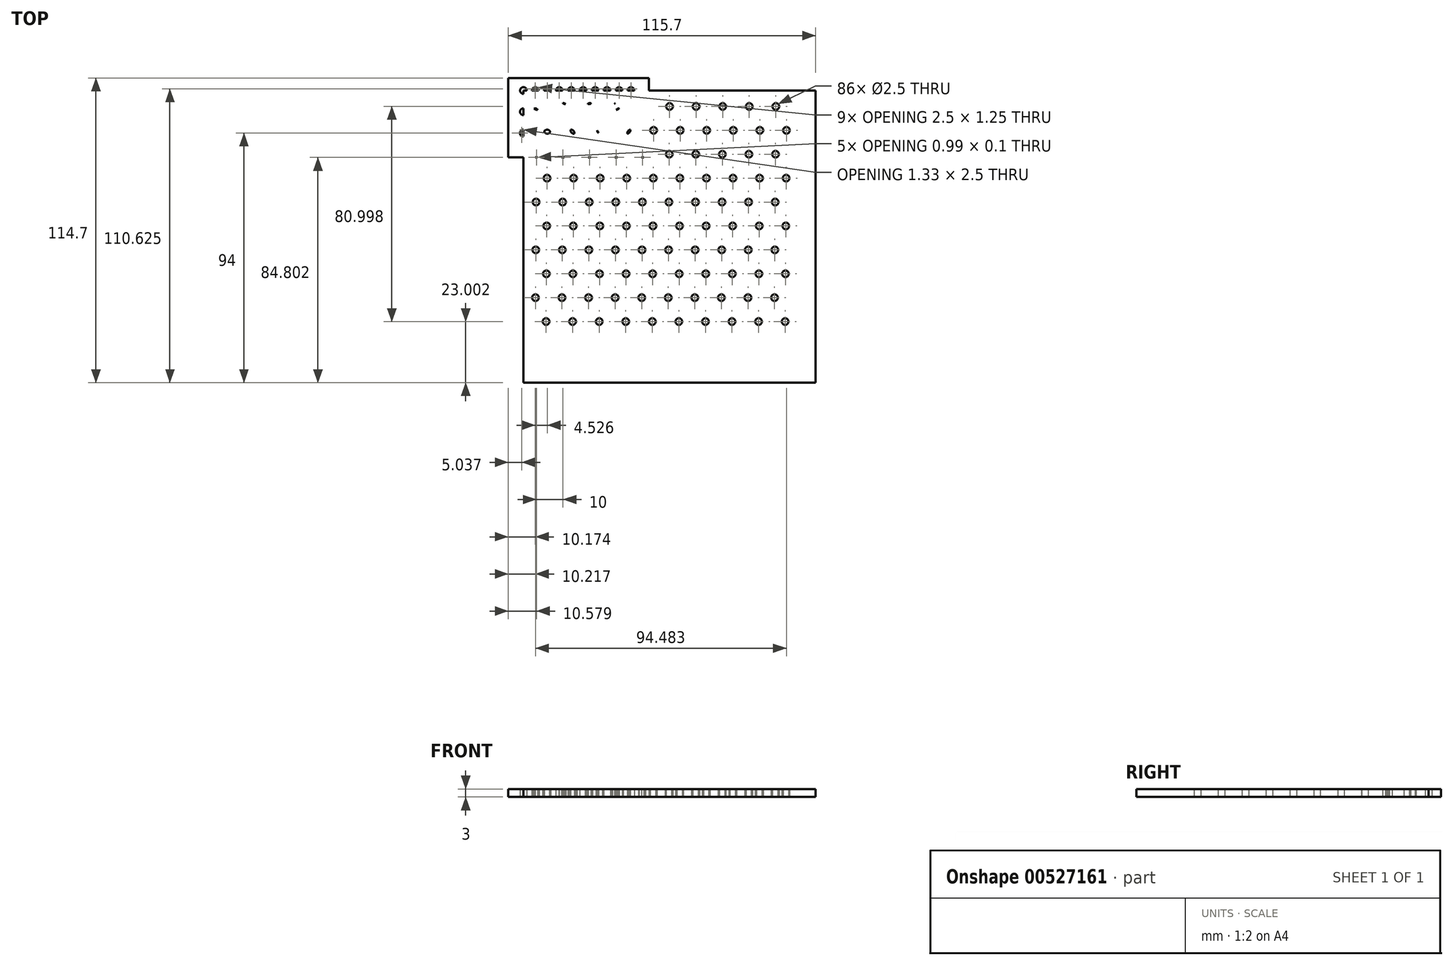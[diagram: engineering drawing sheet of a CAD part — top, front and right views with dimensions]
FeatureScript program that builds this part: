
annotation { "Feature Type Name" : "Feature", "Feature Type Description" : "" }
export const myFeature = defineFeature(function(context is Context, id is Id, definition is map)
    precondition{}
    {
        {
            var Q0;
            Q0=qCreatedBy(makeId("Top.planeOp"),FACE);
            var sketch = newSketch(context, id + "F0", { "sketchPlane" : qUnion([Q0])});
            skLineSegment(sketch, "E0.bottom", {"start": v(0, 0) * mm, "end": v(110, 0) * mm});
            skLineSegment(sketch, "E0.top", {"start": v(0, -110) * mm, "end": v(110, -110) * mm});
            skLineSegment(sketch, "E0.left", {"start": v(0, 0) * mm, "end": v(0, -110) * mm});
            skLineSegment(sketch, "E0.right", {"start": v(110, 0) * mm, "end": v(110, -110) * mm});
            skCircle(sketch, "E1", {"center": v(5, -6) * mm, "radius": 1.25 * mm});
            skCircle(sketch, "E2", {"center": v(9, -15) * mm, "radius": 1.25 * mm});
            skCircle(sketch, "E3", {"center": v(17.21, -30.05) * mm, "radius": 1.25 * mm});
            skCircle(sketch, "E4", {"center": v(38.99, -29.06) * mm, "radius": 1.25 * mm});
            skCircle(sketch, "E5.1.0.0", {"center": v(19, -15) * mm, "radius": 1.25 * mm});
            skCircle(sketch, "E5.1.0.1", {"center": v(15, -6) * mm, "radius": 1.25 * mm});
            skCircle(sketch, "E5.2.0.0", {"center": v(29, -15) * mm, "radius": 1.25 * mm});
            skCircle(sketch, "E5.2.0.1", {"center": v(25, -6) * mm, "radius": 1.25 * mm});
            skCircle(sketch, "E5.3.0.0", {"center": v(39, -15) * mm, "radius": 1.25 * mm});
            skCircle(sketch, "E5.3.0.1", {"center": v(35, -6) * mm, "radius": 1.25 * mm});
            skCircle(sketch, "E5.4.0.0", {"center": v(49, -15) * mm, "radius": 1.25 * mm});
            skCircle(sketch, "E5.4.0.1", {"center": v(45, -6) * mm, "radius": 1.25 * mm});
            skCircle(sketch, "E5.5.0.0", {"center": v(59, -15) * mm, "radius": 1.25 * mm});
            skCircle(sketch, "E5.5.0.1", {"center": v(55, -6) * mm, "radius": 1.25 * mm});
            skCircle(sketch, "E5.6.0.0", {"center": v(69, -15) * mm, "radius": 1.25 * mm});
            skCircle(sketch, "E5.6.0.1", {"center": v(65, -6) * mm, "radius": 1.25 * mm});
            skCircle(sketch, "E5.7.0.0", {"center": v(79, -15) * mm, "radius": 1.25 * mm});
            skCircle(sketch, "E5.7.0.1", {"center": v(75, -6) * mm, "radius": 1.25 * mm});
            skCircle(sketch, "E5.8.0.0", {"center": v(89, -15) * mm, "radius": 1.25 * mm});
            skCircle(sketch, "E5.8.0.1", {"center": v(85, -6) * mm, "radius": 1.25 * mm});
            skCircle(sketch, "E5.9.0.0", {"center": v(99, -15) * mm, "radius": 1.25 * mm});
            skCircle(sketch, "E5.9.0.1", {"center": v(95, -6) * mm, "radius": 1.25 * mm});
            skLineSegment(sketch, "E5.direction1", {"start": v(9, -15) * mm, "end": v(19, -15) * mm, "construction": true});
            skCircle(sketch, "E6.1.0.0", {"center": v(78.88, -33) * mm, "radius": 1.25 * mm});
            skCircle(sketch, "E6.1.0.1", {"center": v(74.88, -24) * mm, "radius": 1.25 * mm});
            skCircle(sketch, "E6.1.0.2", {"center": v(68.88, -33) * mm, "radius": 1.25 * mm});
            skCircle(sketch, "E6.1.0.3", {"center": v(8.88, -33) * mm, "radius": 1.25 * mm});
            skLineSegment(sketch, "E6.1.0.4", {"start": v(8.88, -33) * mm, "end": v(18.88, -33) * mm, "construction": true});
            skCircle(sketch, "E6.1.0.5", {"center": v(94.88, -24) * mm, "radius": 1.25 * mm});
            skCircle(sketch, "E6.1.0.6", {"center": v(28.88, -33) * mm, "radius": 1.25 * mm});
            skCircle(sketch, "E6.1.0.7", {"center": v(44.88, -24) * mm, "radius": 1.25 * mm});
            skCircle(sketch, "E6.1.0.8", {"center": v(84.88, -24) * mm, "radius": 1.25 * mm});
            skCircle(sketch, "E6.1.0.9", {"center": v(58.88, -33) * mm, "radius": 1.25 * mm});
            skCircle(sketch, "E6.1.0.10", {"center": v(38.88, -33) * mm, "radius": 1.25 * mm});
            skCircle(sketch, "E6.1.0.11", {"center": v(24.88, -24) * mm, "radius": 1.25 * mm});
            skCircle(sketch, "E6.1.0.12", {"center": v(14.88, -24) * mm, "radius": 1.25 * mm});
            skCircle(sketch, "E6.1.0.13", {"center": v(48.88, -33) * mm, "radius": 1.25 * mm});
            skCircle(sketch, "E6.1.0.14", {"center": v(88.88, -33) * mm, "radius": 1.25 * mm});
            skCircle(sketch, "E6.1.0.15", {"center": v(64.88, -24) * mm, "radius": 1.25 * mm});
            skCircle(sketch, "E6.1.0.16", {"center": v(98.88, -33) * mm, "radius": 1.25 * mm});
            skCircle(sketch, "E6.1.0.17", {"center": v(34.88, -24) * mm, "radius": 1.25 * mm});
            skCircle(sketch, "E6.1.0.18", {"center": v(54.88, -24) * mm, "radius": 1.25 * mm});
            skCircle(sketch, "E6.1.0.19", {"center": v(18.88, -33) * mm, "radius": 1.25 * mm});
            skCircle(sketch, "E6.1.0.20", {"center": v(4.88, -24) * mm, "radius": 1.25 * mm});
            skCircle(sketch, "E6.2.0.0", {"center": v(78.76, -51) * mm, "radius": 1.25 * mm});
            skCircle(sketch, "E6.2.0.1", {"center": v(74.76, -42) * mm, "radius": 1.25 * mm});
            skCircle(sketch, "E6.2.0.2", {"center": v(68.76, -51) * mm, "radius": 1.25 * mm});
            skCircle(sketch, "E6.2.0.3", {"center": v(8.76, -51) * mm, "radius": 1.25 * mm});
            skLineSegment(sketch, "E6.2.0.4", {"start": v(8.76, -51) * mm, "end": v(18.76, -51) * mm, "construction": true});
            skCircle(sketch, "E6.2.0.5", {"center": v(94.76, -42) * mm, "radius": 1.25 * mm});
            skCircle(sketch, "E6.2.0.6", {"center": v(28.76, -51) * mm, "radius": 1.25 * mm});
            skCircle(sketch, "E6.2.0.7", {"center": v(44.76, -42) * mm, "radius": 1.25 * mm});
            skCircle(sketch, "E6.2.0.8", {"center": v(84.76, -42) * mm, "radius": 1.25 * mm});
            skCircle(sketch, "E6.2.0.9", {"center": v(58.76, -51) * mm, "radius": 1.25 * mm});
            skCircle(sketch, "E6.2.0.10", {"center": v(38.76, -51) * mm, "radius": 1.25 * mm});
            skCircle(sketch, "E6.2.0.11", {"center": v(24.76, -42) * mm, "radius": 1.25 * mm});
            skCircle(sketch, "E6.2.0.12", {"center": v(14.76, -42) * mm, "radius": 1.25 * mm});
            skCircle(sketch, "E6.2.0.13", {"center": v(48.76, -51) * mm, "radius": 1.25 * mm});
            skCircle(sketch, "E6.2.0.14", {"center": v(88.76, -51) * mm, "radius": 1.25 * mm});
            skCircle(sketch, "E6.2.0.15", {"center": v(64.76, -42) * mm, "radius": 1.25 * mm});
            skCircle(sketch, "E6.2.0.16", {"center": v(98.76, -51) * mm, "radius": 1.25 * mm});
            skCircle(sketch, "E6.2.0.17", {"center": v(34.76, -42) * mm, "radius": 1.25 * mm});
            skCircle(sketch, "E6.2.0.18", {"center": v(54.76, -42) * mm, "radius": 1.25 * mm});
            skCircle(sketch, "E6.2.0.19", {"center": v(18.76, -51) * mm, "radius": 1.25 * mm});
            skCircle(sketch, "E6.2.0.20", {"center": v(4.76, -42) * mm, "radius": 1.25 * mm});
            skCircle(sketch, "E6.3.0.0", {"center": v(78.64, -69) * mm, "radius": 1.25 * mm});
            skCircle(sketch, "E6.3.0.1", {"center": v(74.64, -60) * mm, "radius": 1.25 * mm});
            skCircle(sketch, "E6.3.0.2", {"center": v(68.64, -69) * mm, "radius": 1.25 * mm});
            skCircle(sketch, "E6.3.0.3", {"center": v(8.64, -69) * mm, "radius": 1.25 * mm});
            skLineSegment(sketch, "E6.3.0.4", {"start": v(8.64, -69) * mm, "end": v(18.64, -69) * mm, "construction": true});
            skCircle(sketch, "E6.3.0.5", {"center": v(94.64, -60) * mm, "radius": 1.25 * mm});
            skCircle(sketch, "E6.3.0.6", {"center": v(28.64, -69) * mm, "radius": 1.25 * mm});
            skCircle(sketch, "E6.3.0.7", {"center": v(44.64, -60) * mm, "radius": 1.25 * mm});
            skCircle(sketch, "E6.3.0.8", {"center": v(84.64, -60) * mm, "radius": 1.25 * mm});
            skCircle(sketch, "E6.3.0.9", {"center": v(58.64, -69) * mm, "radius": 1.25 * mm});
            skCircle(sketch, "E6.3.0.10", {"center": v(38.64, -69) * mm, "radius": 1.25 * mm});
            skCircle(sketch, "E6.3.0.11", {"center": v(24.64, -60) * mm, "radius": 1.25 * mm});
            skCircle(sketch, "E6.3.0.12", {"center": v(14.64, -60) * mm, "radius": 1.25 * mm});
            skCircle(sketch, "E6.3.0.13", {"center": v(48.64, -69) * mm, "radius": 1.25 * mm});
            skCircle(sketch, "E6.3.0.14", {"center": v(88.64, -69) * mm, "radius": 1.25 * mm});
            skCircle(sketch, "E6.3.0.15", {"center": v(64.64, -60) * mm, "radius": 1.25 * mm});
            skCircle(sketch, "E6.3.0.16", {"center": v(98.64, -69) * mm, "radius": 1.25 * mm});
            skCircle(sketch, "E6.3.0.17", {"center": v(34.64, -60) * mm, "radius": 1.25 * mm});
            skCircle(sketch, "E6.3.0.18", {"center": v(54.64, -60) * mm, "radius": 1.25 * mm});
            skCircle(sketch, "E6.3.0.19", {"center": v(18.64, -69) * mm, "radius": 1.25 * mm});
            skCircle(sketch, "E6.3.0.20", {"center": v(4.64, -60) * mm, "radius": 1.25 * mm});
            skCircle(sketch, "E6.4.0.0", {"center": v(78.52, -87) * mm, "radius": 1.25 * mm});
            skCircle(sketch, "E6.4.0.1", {"center": v(74.52, -78) * mm, "radius": 1.25 * mm});
            skCircle(sketch, "E6.4.0.2", {"center": v(68.52, -87) * mm, "radius": 1.25 * mm});
            skCircle(sketch, "E6.4.0.3", {"center": v(8.52, -87) * mm, "radius": 1.25 * mm});
            skLineSegment(sketch, "E6.4.0.4", {"start": v(8.52, -87) * mm, "end": v(18.52, -87) * mm, "construction": true});
            skCircle(sketch, "E6.4.0.5", {"center": v(94.52, -78) * mm, "radius": 1.25 * mm});
            skCircle(sketch, "E6.4.0.6", {"center": v(28.52, -87) * mm, "radius": 1.25 * mm});
            skCircle(sketch, "E6.4.0.7", {"center": v(44.52, -78) * mm, "radius": 1.25 * mm});
            skCircle(sketch, "E6.4.0.8", {"center": v(84.52, -78) * mm, "radius": 1.25 * mm});
            skCircle(sketch, "E6.4.0.9", {"center": v(58.52, -87) * mm, "radius": 1.25 * mm});
            skCircle(sketch, "E6.4.0.10", {"center": v(38.52, -87) * mm, "radius": 1.25 * mm});
            skCircle(sketch, "E6.4.0.11", {"center": v(24.52, -78) * mm, "radius": 1.25 * mm});
            skCircle(sketch, "E6.4.0.12", {"center": v(14.52, -78) * mm, "radius": 1.25 * mm});
            skCircle(sketch, "E6.4.0.13", {"center": v(48.52, -87) * mm, "radius": 1.25 * mm});
            skCircle(sketch, "E6.4.0.14", {"center": v(88.52, -87) * mm, "radius": 1.25 * mm});
            skCircle(sketch, "E6.4.0.15", {"center": v(64.52, -78) * mm, "radius": 1.25 * mm});
            skCircle(sketch, "E6.4.0.16", {"center": v(98.52, -87) * mm, "radius": 1.25 * mm});
            skCircle(sketch, "E6.4.0.17", {"center": v(34.52, -78) * mm, "radius": 1.25 * mm});
            skCircle(sketch, "E6.4.0.18", {"center": v(54.52, -78) * mm, "radius": 1.25 * mm});
            skCircle(sketch, "E6.4.0.19", {"center": v(18.52, -87) * mm, "radius": 1.25 * mm});
            skCircle(sketch, "E6.4.0.20", {"center": v(4.52, -78) * mm, "radius": 1.25 * mm});
            skLineSegment(sketch, "E6.direction1", {"start": v(9, -15) * mm, "end": v(8.88, -33) * mm, "construction": true});
            skSolve(sketch);
        }
        {
            var Q0;
            Q0=qCreatedBy(makeId("Top.planeOp"),FACE);
            var sketch = newSketch(context, id + "F1", { "sketchPlane" : qUnion([Q0])});
            skCircle(sketch, "E7", {"center": v(0, 0) * mm, "radius": 1.25 * mm});
            skCircle(sketch, "E8", {"center": v(4.47, 0) * mm, "radius": 1.25 * mm});
            skCircle(sketch, "E9", {"center": v(2.5, -4.33) * mm, "radius": 1.25 * mm});
            skCircle(sketch, "E10", {"center": v(6.71, -3.87) * mm, "radius": 1.25 * mm});
            skCircle(sketch, "E11.1.0.0", {"center": v(13.47, 0) * mm, "radius": 1.25 * mm});
            skCircle(sketch, "E11.1.0.1", {"center": v(9, 0) * mm, "radius": 1.25 * mm});
            skCircle(sketch, "E11.1.0.2", {"center": v(11.5, -4.33) * mm, "radius": 1.25 * mm});
            skCircle(sketch, "E11.1.0.3", {"center": v(15.71, -3.87) * mm, "radius": 1.25 * mm});
            skCircle(sketch, "E11.2.0.0", {"center": v(22.47, 0) * mm, "radius": 1.25 * mm});
            skCircle(sketch, "E11.2.0.1", {"center": v(18, 0) * mm, "radius": 1.25 * mm});
            skCircle(sketch, "E11.2.0.2", {"center": v(20.5, -4.33) * mm, "radius": 1.25 * mm});
            skCircle(sketch, "E11.2.0.3", {"center": v(24.71, -3.87) * mm, "radius": 1.25 * mm});
            skCircle(sketch, "E11.3.0.0", {"center": v(31.47, 0) * mm, "radius": 1.25 * mm});
            skCircle(sketch, "E11.3.0.1", {"center": v(27, 0) * mm, "radius": 1.25 * mm});
            skCircle(sketch, "E11.3.0.2", {"center": v(29.5, -4.33) * mm, "radius": 1.25 * mm});
            skCircle(sketch, "E11.3.0.3", {"center": v(33.71, -3.87) * mm, "radius": 1.25 * mm});
            skCircle(sketch, "E11.4.0.0", {"center": v(40.47, 0) * mm, "radius": 1.25 * mm});
            skCircle(sketch, "E11.4.0.1", {"center": v(36, 0) * mm, "radius": 1.25 * mm});
            skCircle(sketch, "E11.4.0.2", {"center": v(38.5, -4.33) * mm, "radius": 1.25 * mm});
            skCircle(sketch, "E11.4.0.3", {"center": v(42.71, -3.87) * mm, "radius": 1.25 * mm});
            skLineSegment(sketch, "E11.direction1", {"start": v(2.5, -4.33) * mm, "end": v(11.5, -4.33) * mm, "construction": true});
            skCircle(sketch, "E12.1.0.0", {"center": v(40.44, -8) * mm, "radius": 1.25 * mm});
            skCircle(sketch, "E12.1.0.1", {"center": v(26.96, -8) * mm, "radius": 1.25 * mm});
            skCircle(sketch, "E12.1.0.2", {"center": v(29.46, -12.33) * mm, "radius": 1.25 * mm});
            skCircle(sketch, "E12.1.0.3", {"center": v(33.67, -11.87) * mm, "radius": 1.25 * mm});
            skLineSegment(sketch, "E12.1.0.4", {"start": v(2.46, -12.33) * mm, "end": v(11.46, -12.33) * mm, "construction": true});
            skCircle(sketch, "E12.1.0.5", {"center": v(4.44, -8) * mm, "radius": 1.25 * mm});
            skCircle(sketch, "E12.1.0.6", {"center": v(38.46, -12.33) * mm, "radius": 1.25 * mm});
            skCircle(sketch, "E12.1.0.7", {"center": v(-0.04, -8) * mm, "radius": 1.25 * mm});
            skCircle(sketch, "E12.1.0.8", {"center": v(2.46, -12.33) * mm, "radius": 1.25 * mm});
            skCircle(sketch, "E12.1.0.9", {"center": v(6.67, -11.87) * mm, "radius": 1.25 * mm});
            skCircle(sketch, "E12.1.0.10", {"center": v(13.44, -8) * mm, "radius": 1.25 * mm});
            skCircle(sketch, "E12.1.0.11", {"center": v(8.96, -8) * mm, "radius": 1.25 * mm});
            skCircle(sketch, "E12.1.0.12", {"center": v(11.46, -12.33) * mm, "radius": 1.25 * mm});
            skCircle(sketch, "E12.1.0.13", {"center": v(15.67, -11.87) * mm, "radius": 1.25 * mm});
            skCircle(sketch, "E12.1.0.14", {"center": v(22.44, -8) * mm, "radius": 1.25 * mm});
            skCircle(sketch, "E12.1.0.15", {"center": v(17.96, -8) * mm, "radius": 1.25 * mm});
            skCircle(sketch, "E12.1.0.16", {"center": v(42.67, -11.87) * mm, "radius": 1.25 * mm});
            skCircle(sketch, "E12.1.0.17", {"center": v(20.46, -12.33) * mm, "radius": 1.25 * mm});
            skCircle(sketch, "E12.1.0.18", {"center": v(24.67, -11.87) * mm, "radius": 1.25 * mm});
            skCircle(sketch, "E12.1.0.19", {"center": v(35.96, -8) * mm, "radius": 1.25 * mm});
            skCircle(sketch, "E12.1.0.20", {"center": v(31.44, -8) * mm, "radius": 1.25 * mm});
            skCircle(sketch, "E12.2.0.0", {"center": v(40.4, -16) * mm, "radius": 1.25 * mm});
            skCircle(sketch, "E12.2.0.1", {"center": v(26.92, -16) * mm, "radius": 1.25 * mm});
            skCircle(sketch, "E12.2.0.2", {"center": v(29.42, -20.33) * mm, "radius": 1.25 * mm});
            skCircle(sketch, "E12.2.0.3", {"center": v(33.64, -19.87) * mm, "radius": 1.25 * mm});
            skLineSegment(sketch, "E12.2.0.4", {"start": v(2.42, -20.33) * mm, "end": v(11.42, -20.33) * mm, "construction": true});
            skCircle(sketch, "E12.2.0.5", {"center": v(4.4, -16) * mm, "radius": 1.25 * mm});
            skCircle(sketch, "E12.2.0.6", {"center": v(38.42, -20.33) * mm, "radius": 1.25 * mm});
            skCircle(sketch, "E12.2.0.7", {"center": v(-0.08, -16) * mm, "radius": 1.25 * mm});
            skCircle(sketch, "E12.2.0.8", {"center": v(2.42, -20.33) * mm, "radius": 1.25 * mm});
            skCircle(sketch, "E12.2.0.9", {"center": v(6.64, -19.87) * mm, "radius": 1.25 * mm});
            skCircle(sketch, "E12.2.0.10", {"center": v(13.4, -16) * mm, "radius": 1.25 * mm});
            skCircle(sketch, "E12.2.0.11", {"center": v(8.92, -16) * mm, "radius": 1.25 * mm});
            skCircle(sketch, "E12.2.0.12", {"center": v(11.42, -20.33) * mm, "radius": 1.25 * mm});
            skCircle(sketch, "E12.2.0.13", {"center": v(15.64, -19.87) * mm, "radius": 1.25 * mm});
            skCircle(sketch, "E12.2.0.14", {"center": v(22.4, -16) * mm, "radius": 1.25 * mm});
            skCircle(sketch, "E12.2.0.15", {"center": v(17.92, -16) * mm, "radius": 1.25 * mm});
            skCircle(sketch, "E12.2.0.16", {"center": v(42.64, -19.87) * mm, "radius": 1.25 * mm});
            skCircle(sketch, "E12.2.0.17", {"center": v(20.42, -20.33) * mm, "radius": 1.25 * mm});
            skCircle(sketch, "E12.2.0.18", {"center": v(24.64, -19.87) * mm, "radius": 1.25 * mm});
            skCircle(sketch, "E12.2.0.19", {"center": v(35.92, -16) * mm, "radius": 1.25 * mm});
            skCircle(sketch, "E12.2.0.20", {"center": v(31.4, -16) * mm, "radius": 1.25 * mm});
            skLineSegment(sketch, "E12.direction1", {"start": v(2.5, -4.33) * mm, "end": v(2.46, -12.33) * mm, "construction": true});
            skLineSegment(sketch, "E13.bottom", {"start": v(-5.7, 4.7) * mm, "end": v(47.28, 4.7) * mm});
            skLineSegment(sketch, "E13.top", {"start": v(-5.7, -25.15) * mm, "end": v(47.28, -25.15) * mm});
            skLineSegment(sketch, "E13.left", {"start": v(-5.7, 4.7) * mm, "end": v(-5.7, -25.15) * mm});
            skLineSegment(sketch, "E13.right", {"start": v(47.28, 4.7) * mm, "end": v(47.28, -25.15) * mm});
            skSolve(sketch);
        }
        {
            var Q0;
            Q0 = qSketchRegion(id + "F1", true);
            extrude(context, id + "F2", {"entities" : qUnion([Q0]), "depth" : 3 * mm, "offsetDistance" : 25 * mm});
        }
        {
            var Q0;
            Q0=makeQuery(id+"F0.imprint","IMPRINT",FACE,{"disambiguationData":[TD([[makeQuery(id+"F0.imprint","IMPRINT",EDGE,{"derivedFrom":sQuery(id+"F0.wireOp",EDGE,"E0.bottom")}),-1.0]])]});
            var Q1;
            Q1=makeQuery(id+"F0.imprint","IMPRINT",FACE,{"disambiguationData":[TD([[makeQuery(id+"F0.imprint","IMPRINT",EDGE,{"derivedFrom":sQuery(id+"F0.wireOp",EDGE,"E4")}),1.0]])]});
            var Q2;
            Q2=makeQuery(id+"F0.imprint","IMPRINT",FACE,{"disambiguationData":[TD([[makeQuery(id+"F0.imprint","IMPRINT",EDGE,{"derivedFrom":sQuery(id+"F0.wireOp",EDGE,"E3")}),1.0]])]});
            extrude(context, id + "F3", {"entities" : qUnion([Q0, Q1, Q2]), "operationType" : NewBodyOperationType.ADD, "depth" : 3 * mm, "offsetDistance" : 25 * mm});
        }
    });
